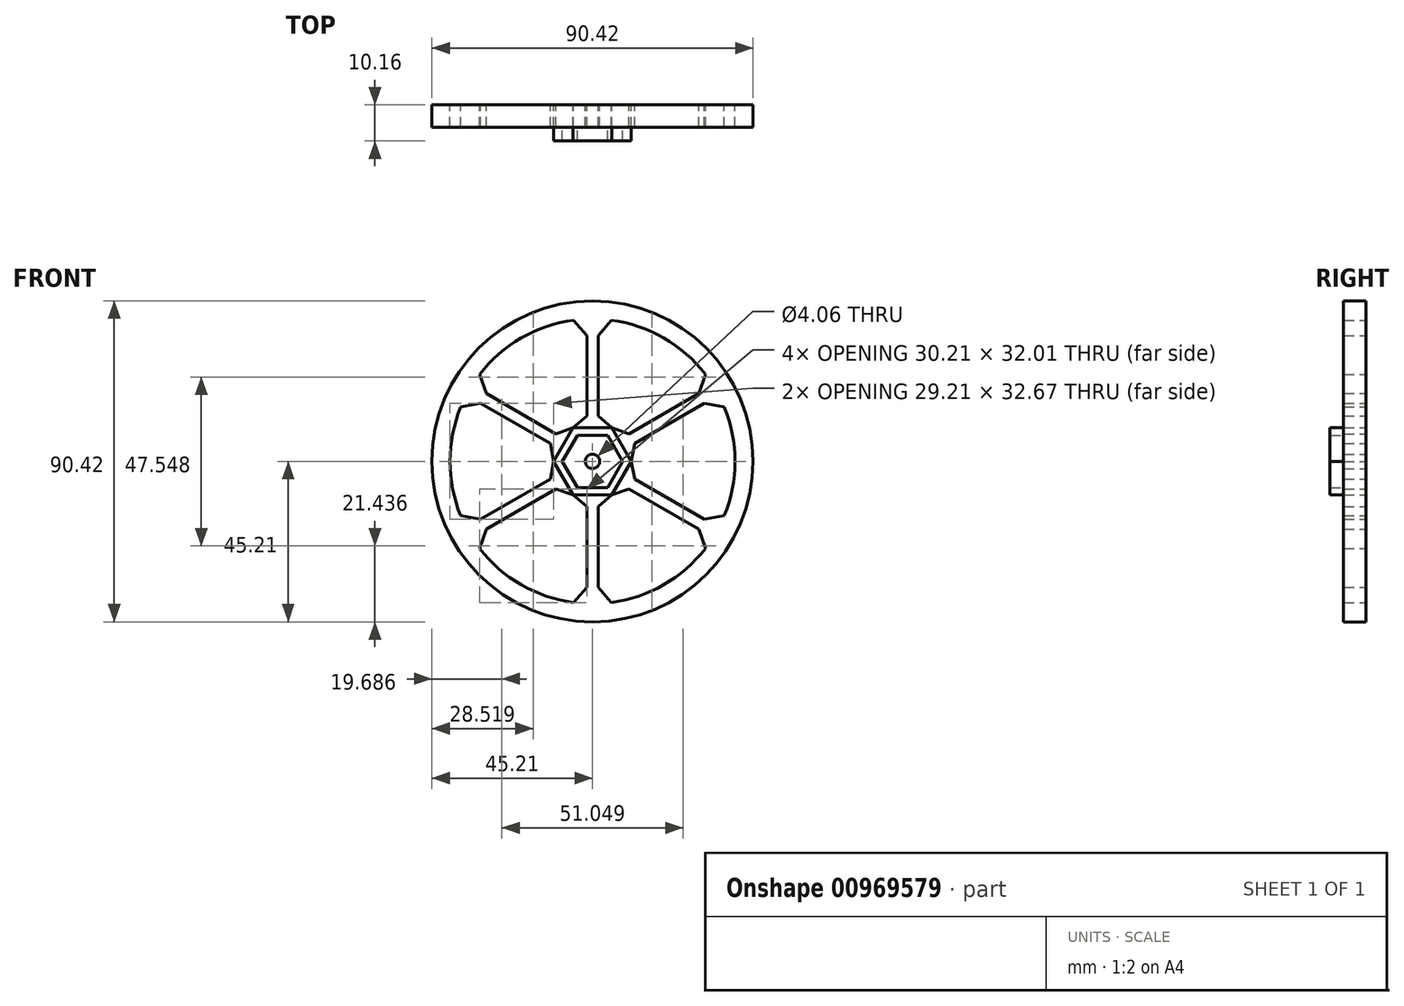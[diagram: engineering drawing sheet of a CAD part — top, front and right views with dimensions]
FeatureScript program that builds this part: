
annotation { "Feature Type Name" : "Feature", "Feature Type Description" : "" }
export const myFeature = defineFeature(function(context is Context, id is Id, definition is map)
    precondition{}
    {
        {
            var Q0;
            Q0=qCreatedBy(makeId("Front.planeOp"),FACE);
            var sketch = newSketch(context, id + "F0", { "sketchPlane" : qUnion([Q0])});
            skCircle(sketch, "E0", {"center": v(0, 0) * mm, "radius": 45.21 * mm});
            skCircle(sketch, "E1", {"center": v(0, 0) * mm, "radius": 40.13 * mm});
            skCircle(sketch, "E2", {"center": v(0, 0) * mm, "radius": 2.03 * mm});
            skLineSegment(sketch, "E3.0", {"start": v(4.25, -7.37) * mm, "end": v(-4.25, -7.37) * mm});
            skLineSegment(sketch, "E3.1", {"start": v(-4.25, -7.37) * mm, "end": v(-8.5, 0) * mm});
            skLineSegment(sketch, "E3.2", {"start": v(-8.5, 0) * mm, "end": v(-4.25, 7.37) * mm});
            skLineSegment(sketch, "E3.3", {"start": v(-4.25, 7.37) * mm, "end": v(4.25, 7.37) * mm});
            skLineSegment(sketch, "E3.4", {"start": v(4.25, 7.37) * mm, "end": v(8.5, 0) * mm});
            skLineSegment(sketch, "E3.5", {"start": v(8.5, 0) * mm, "end": v(4.25, -7.37) * mm});
            skPoint(sketch, "E3.0.midPoint", {"position": v(0, -7.37) * mm});
            skLineSegment(sketch, "E4.0", {"start": v(5.46, -9.45) * mm, "end": v(-5.46, -9.45) * mm});
            skLineSegment(sketch, "E4.1", {"start": v(-5.46, -9.45) * mm, "end": v(-10.92, 0) * mm});
            skLineSegment(sketch, "E4.2", {"start": v(-10.92, 0) * mm, "end": v(-5.46, 9.45) * mm});
            skLineSegment(sketch, "E4.3", {"start": v(-5.46, 9.45) * mm, "end": v(5.46, 9.45) * mm});
            skLineSegment(sketch, "E4.4", {"start": v(5.46, 9.45) * mm, "end": v(10.92, 0) * mm});
            skLineSegment(sketch, "E4.5", {"start": v(10.92, 0) * mm, "end": v(5.46, -9.45) * mm});
            skPoint(sketch, "E4.0.midPoint", {"position": v(0, -9.45) * mm});
            skLineSegment(sketch, "E5", {"start": v(-5.46, 9.45) * mm, "end": v(-4.25, 7.37) * mm});
            skLineSegment(sketch, "E6", {"start": v(5.46, 9.45) * mm, "end": v(4.25, 7.37) * mm});
            skLineSegment(sketch, "E7", {"start": v(10.92, 0) * mm, "end": v(8.5, 0) * mm});
            skLineSegment(sketch, "E8", {"start": v(5.46, -9.45) * mm, "end": v(4.25, -7.37) * mm});
            skLineSegment(sketch, "E9", {"start": v(-5.46, -9.45) * mm, "end": v(-4.25, -7.37) * mm});
            skLineSegment(sketch, "E10", {"start": v(-10.92, 0) * mm, "end": v(-8.5, 0) * mm});
            skLineSegment(sketch, "E11", {"start": v(-5.46, 9.45) * mm, "end": v(-1.59, 12.79) * mm});
            skLineSegment(sketch, "E12.MirrorCS", {"start": v(5.46, 9.45) * mm, "end": v(1.59, 12.79) * mm});
            skLineSegment(sketch, "E13", {"start": v(-1.59, 35.42) * mm, "end": v(-5.31, 39.78) * mm});
            skLineSegment(sketch, "E14.MirrorCS", {"start": v(1.59, 35.42) * mm, "end": v(5.31, 39.78) * mm});
            skLineSegment(sketch, "E15", {"start": v(-1.59, 35.42) * mm, "end": v(-1.59, 12.79) * mm});
            skLineSegment(sketch, "E16", {"start": v(1.59, 35.42) * mm, "end": v(1.59, 12.79) * mm});
            skLineSegment(sketch, "E17.MirrorCS", {"start": v(5.46, -9.45) * mm, "end": v(1.59, -12.79) * mm});
            skLineSegment(sketch, "E18.MirrorCS", {"start": v(-5.46, -9.45) * mm, "end": v(-1.59, -12.79) * mm});
            skLineSegment(sketch, "E19.MirrorCS", {"start": v(-1.59, -35.42) * mm, "end": v(-1.59, -12.79) * mm});
            skLineSegment(sketch, "E20.MirrorCS", {"start": v(1.59, -35.42) * mm, "end": v(1.59, -12.79) * mm});
            skLineSegment(sketch, "E21.MirrorCS", {"start": v(-1.59, -35.42) * mm, "end": v(-5.31, -39.78) * mm});
            skLineSegment(sketch, "E22.MirrorCS", {"start": v(1.59, -35.42) * mm, "end": v(5.31, -39.78) * mm});
            skLineSegment(sketch, "E23.MirrorCS", {"start": v(-5.46, 9.45) * mm, "end": v(-10.28, 7.77) * mm});
            skLineSegment(sketch, "E24.MirrorCS", {"start": v(-10.92, 0) * mm, "end": v(-11.87, 5.02) * mm});
            skLineSegment(sketch, "E25.MirrorCS", {"start": v(-29.88, 19.08) * mm, "end": v(-10.28, 7.77) * mm});
            skLineSegment(sketch, "E26.MirrorCS", {"start": v(-31.47, 16.33) * mm, "end": v(-11.87, 5.02) * mm});
            skLineSegment(sketch, "E27.MirrorCS", {"start": v(-29.88, 19.08) * mm, "end": v(-31.8, 24.49) * mm});
            skLineSegment(sketch, "E28.MirrorCS", {"start": v(-31.47, 16.33) * mm, "end": v(-37.1, 15.29) * mm});
            skLineSegment(sketch, "E29.MirrorCS", {"start": v(-5.46, -9.45) * mm, "end": v(5.46, -9.45) * mm});
            skLineSegment(sketch, "E30.MirrorCS", {"start": v(5.46, 9.45) * mm, "end": v(10.28, 7.77) * mm});
            skLineSegment(sketch, "E31.MirrorCS", {"start": v(10.92, 0) * mm, "end": v(11.87, 5.02) * mm});
            skLineSegment(sketch, "E32.MirrorCS", {"start": v(31.47, 16.33) * mm, "end": v(11.87, 5.02) * mm});
            skLineSegment(sketch, "E33.MirrorCS", {"start": v(29.88, 19.08) * mm, "end": v(10.28, 7.77) * mm});
            skLineSegment(sketch, "E34.MirrorCS", {"start": v(31.47, 16.33) * mm, "end": v(37.1, 15.29) * mm});
            skLineSegment(sketch, "E35.MirrorCS", {"start": v(29.88, 19.08) * mm, "end": v(31.8, 24.49) * mm});
            skLineSegment(sketch, "E36.MirrorCS", {"start": v(10.92, 0) * mm, "end": v(11.87, -5.02) * mm});
            skLineSegment(sketch, "E37.MirrorCS", {"start": v(5.46, -9.45) * mm, "end": v(10.28, -7.77) * mm});
            skLineSegment(sketch, "E38.MirrorCS", {"start": v(31.47, -16.33) * mm, "end": v(11.87, -5.02) * mm});
            skLineSegment(sketch, "E39.MirrorCS", {"start": v(29.88, -19.08) * mm, "end": v(10.28, -7.77) * mm});
            skLineSegment(sketch, "E40.MirrorCS", {"start": v(29.88, -19.08) * mm, "end": v(31.8, -24.49) * mm});
            skLineSegment(sketch, "E41.MirrorCS", {"start": v(31.47, -16.33) * mm, "end": v(37.1, -15.29) * mm});
            skLineSegment(sketch, "E42.MirrorCS", {"start": v(-5.46, -9.45) * mm, "end": v(-10.28, -7.77) * mm});
            skLineSegment(sketch, "E43.MirrorCS", {"start": v(-10.92, 0) * mm, "end": v(-11.87, -5.02) * mm});
            skLineSegment(sketch, "E44.MirrorCS", {"start": v(-29.88, -19.08) * mm, "end": v(-10.28, -7.77) * mm});
            skLineSegment(sketch, "E45.MirrorCS", {"start": v(-31.47, -16.33) * mm, "end": v(-11.87, -5.02) * mm});
            skLineSegment(sketch, "E46.MirrorCS", {"start": v(-29.88, -19.08) * mm, "end": v(-31.8, -24.49) * mm});
            skLineSegment(sketch, "E47.MirrorCS", {"start": v(-31.47, -16.33) * mm, "end": v(-37.1, -15.29) * mm});
            skSolve(sketch);
        }
        {
            var Q0;
            Q0=makeQuery(id+"F0.imprint","IMPRINT",FACE,{"disambiguationData":[TD([[makeQuery(id+"F0.imprint","IMPRINT",EDGE,{"derivedFrom":sQuery(id+"F0.wireOp",EDGE,"E3.2")}),1.0]])]});
            var Q1;
            Q1=makeQuery(id+"F0.imprint","IMPRINT",FACE,{"disambiguationData":[TD([[makeQuery(id+"F0.imprint","IMPRINT",EDGE,{"derivedFrom":sQuery(id+"F0.wireOp",EDGE,"E2")}),-1.0]])]});
            var Q2;
            Q2=makeQuery(id+"F0.imprint","IMPRINT",FACE,{"disambiguationData":[TD([[makeQuery(id+"F0.imprint","IMPRINT",EDGE,{"derivedFrom":sQuery(id+"F0.wireOp",EDGE,"E3.1")}),1.0]])]});
            var Q3;
            Q3=makeQuery(id+"F0.imprint","IMPRINT",FACE,{"disambiguationData":[TD([[makeQuery(id+"F0.imprint","IMPRINT",EDGE,{"derivedFrom":sQuery(id+"F0.wireOp",EDGE,"E3.0")}),1.0]])]});
            var Q4;
            Q4=makeQuery(id+"F0.imprint","IMPRINT",FACE,{"disambiguationData":[TD([[makeQuery(id+"F0.imprint","IMPRINT",EDGE,{"derivedFrom":sQuery(id+"F0.wireOp",EDGE,"E3.5")}),1.0]])]});
            var Q5;
            Q5=makeQuery(id+"F0.imprint","IMPRINT",FACE,{"disambiguationData":[TD([[makeQuery(id+"F0.imprint","IMPRINT",EDGE,{"derivedFrom":sQuery(id+"F0.wireOp",EDGE,"E3.4")}),1.0]])]});
            var Q6;
            Q6=makeQuery(id+"F0.imprint","IMPRINT",FACE,{"disambiguationData":[TD([[makeQuery(id+"F0.imprint","IMPRINT",EDGE,{"derivedFrom":sQuery(id+"F0.wireOp",EDGE,"E3.3")}),1.0]])]});
            var Q7;
            Q7=makeQuery(id+"F0.imprint","IMPRINT",FACE,{"disambiguationData":[TD([[makeQuery(id+"F0.imprint","IMPRINT",EDGE,{"derivedFrom":sQuery(id+"F0.wireOp",EDGE,"E4.3")}),1.0]])]});
            var Q8;
            Q8=makeQuery(id+"F0.imprint","IMPRINT",FACE,{"disambiguationData":[TD([[makeQuery(id+"F0.imprint","IMPRINT",EDGE,{"derivedFrom":sQuery(id+"F0.wireOp",EDGE,"E4.2")}),1.0]])]});
            var Q9;
            Q9=makeQuery(id+"F0.imprint","IMPRINT",FACE,{"disambiguationData":[TD([[makeQuery(id+"F0.imprint","IMPRINT",EDGE,{"derivedFrom":sQuery(id+"F0.wireOp",EDGE,"E4.1")}),1.0]])]});
            var Q10;
            Q10=makeQuery(id+"F0.imprint","IMPRINT",FACE,{"disambiguationData":[TD([[makeQuery(id+"F0.imprint","IMPRINT",EDGE,{"derivedFrom":sQuery(id+"F0.wireOp",EDGE,"E18.MirrorCS")}),1.0]])]});
            var Q11;
            Q11=makeQuery(id+"F0.imprint","IMPRINT",FACE,{"disambiguationData":[TD([[makeQuery(id+"F0.imprint","IMPRINT",EDGE,{"derivedFrom":sQuery(id+"F0.wireOp",EDGE,"E4.5")}),1.0]])]});
            var Q12;
            Q12=makeQuery(id+"F0.imprint","IMPRINT",FACE,{"disambiguationData":[TD([[makeQuery(id+"F0.imprint","IMPRINT",EDGE,{"derivedFrom":sQuery(id+"F0.wireOp",EDGE,"E4.4")}),1.0]])]});
            var Q13;
            Q13=makeQuery(id+"F0.imprint","IMPRINT",FACE,{"disambiguationData":[TD([[makeQuery(id+"F0.imprint","IMPRINT",EDGE,{"derivedFrom":sQuery(id+"F0.wireOp",EDGE,"E0")}),1.0]])]});
            extrude(context, id + "F1", {"entities" : qUnion([Q0, Q1, Q2, Q3, Q4, Q5, Q6, Q7, Q8, Q9, Q10, Q11, Q12, Q13]), "depth" : 6.35 * mm, "offsetDistance" : 25.4 * mm});
        }
        {
            var Q0;
            Q0=makeQuery(id+"F0.imprint","IMPRINT",FACE,{"disambiguationData":[TD([[makeQuery(id+"F0.imprint","IMPRINT",EDGE,{"derivedFrom":sQuery(id+"F0.wireOp",EDGE,"E3.1")}),1.0]])]});
            var Q1;
            Q1=makeQuery(id+"F0.imprint","IMPRINT",FACE,{"disambiguationData":[TD([[makeQuery(id+"F0.imprint","IMPRINT",EDGE,{"derivedFrom":sQuery(id+"F0.wireOp",EDGE,"E3.0")}),1.0]])]});
            var Q2;
            Q2=makeQuery(id+"F0.imprint","IMPRINT",FACE,{"disambiguationData":[TD([[makeQuery(id+"F0.imprint","IMPRINT",EDGE,{"derivedFrom":sQuery(id+"F0.wireOp",EDGE,"E3.5")}),1.0]])]});
            var Q3;
            Q3=makeQuery(id+"F0.imprint","IMPRINT",FACE,{"disambiguationData":[TD([[makeQuery(id+"F0.imprint","IMPRINT",EDGE,{"derivedFrom":sQuery(id+"F0.wireOp",EDGE,"E3.4")}),1.0]])]});
            var Q4;
            Q4=makeQuery(id+"F0.imprint","IMPRINT",FACE,{"disambiguationData":[TD([[makeQuery(id+"F0.imprint","IMPRINT",EDGE,{"derivedFrom":sQuery(id+"F0.wireOp",EDGE,"E3.3")}),1.0]])]});
            var Q5;
            Q5=makeQuery(id+"F0.imprint","IMPRINT",FACE,{"disambiguationData":[TD([[makeQuery(id+"F0.imprint","IMPRINT",EDGE,{"derivedFrom":sQuery(id+"F0.wireOp",EDGE,"E3.2")}),1.0]])]});
            extrude(context, id + "F2", {"entities" : qUnion([Q0, Q1, Q2, Q3, Q4, Q5]), "operationType" : NewBodyOperationType.ADD, "depth" : 10.16 * mm, "offsetDistance" : 25.4 * mm});
        }
    });
